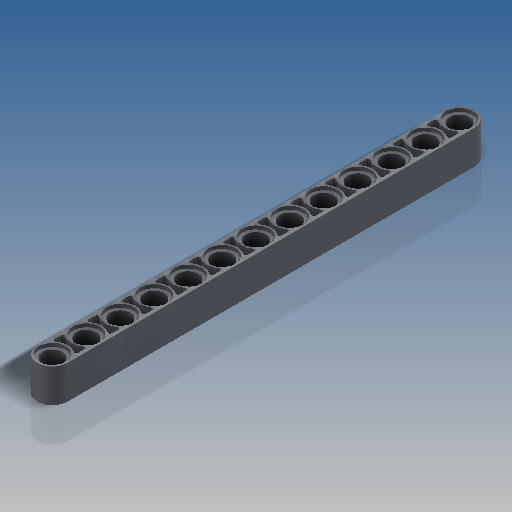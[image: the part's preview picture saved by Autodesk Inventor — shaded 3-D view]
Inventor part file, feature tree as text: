
AUTODESK INVENTOR PART (.ipt)
format: ipt  version: 2018.3 (Build 223284000, 284)  size: 547,328 bytes
history: native  units: mm
features: extrude x3, sketch x2, projected_geometry x2, mirror x1, fillet x1
ambient origin geometry x8: Origin, YZ Plane, XZ Plane, XY Plane, X Axis, Y Axis, Z Axis, Center Point
bodies: Solid1 (feature_tree)
feature tree (9):
  extrude  "Extrusion1"  Depth=7.2mm
  sketch  "Sketch6"  dims[d41=0.8mm d42=0.0mm d43=3.1mm d44=0.0mm d48=96.0mm d49=6.4mm d50=4.8mm d51=8.0mm d52=0.8mm d53=120.0mm d55=8.0mm d56=10.0mm d58=10.0mm d60=0.4mm d61=0.1mm]
  extrude  "Extrusion7"  Depth=3.1mm TaperAngle=0.0deg
  extrude  "Extrusion8"  Depth=0.1mm
  mirror  "Mirror1"
  fillet  "Fillet2"  Radius=6.4mm
  sketch  "Sketch1"  dims[d14=8.0mm d15=0.0mm d32=7.2mm]
  projected_geometry  "Projected Loop3"
  projected_geometry  "Projected Loop4"
